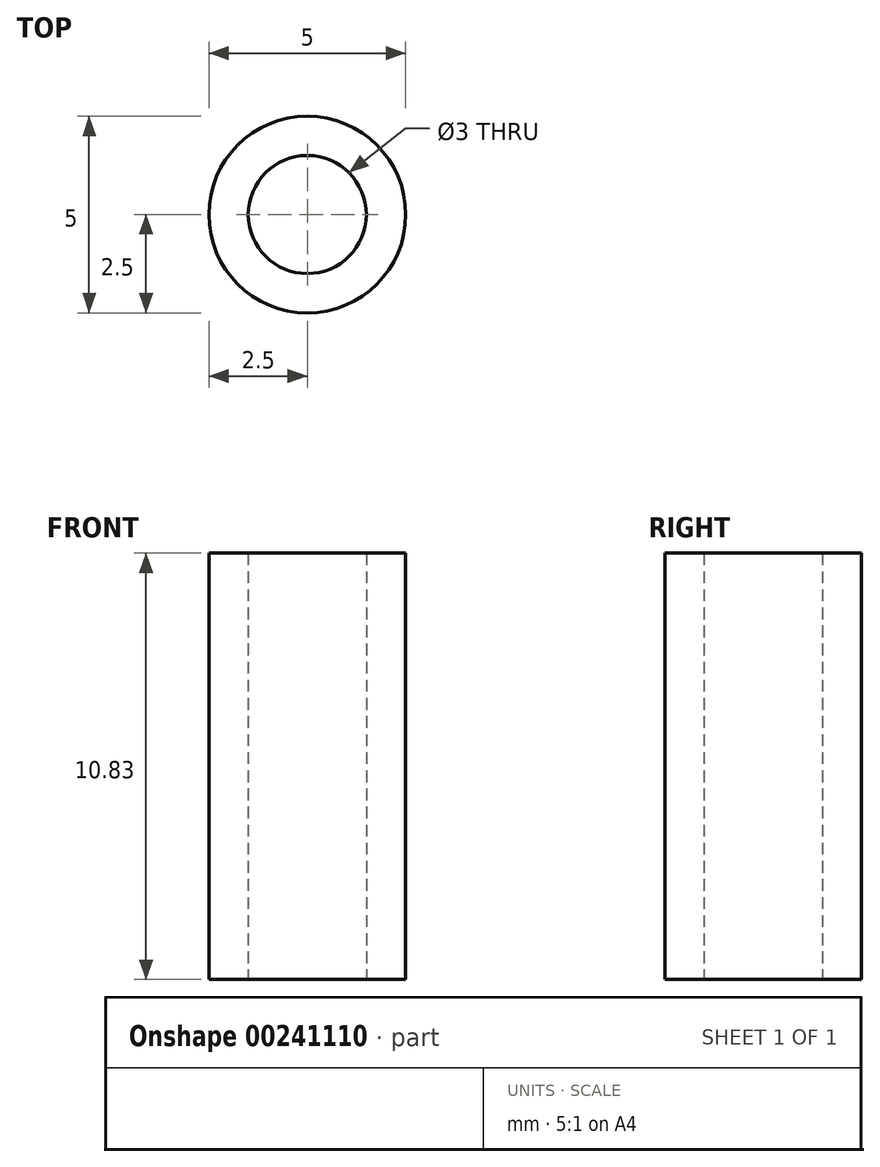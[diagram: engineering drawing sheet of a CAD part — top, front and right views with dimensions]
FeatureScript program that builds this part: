
annotation { "Feature Type Name" : "Feature", "Feature Type Description" : "" }
export const myFeature = defineFeature(function(context is Context, id is Id, definition is map)
    precondition{}
    {
        {
            var Q0;
            Q0=qCreatedBy(makeId("Top.planeOp"),FACE);
            var sketch = newSketch(context, id + "F0", { "sketchPlane" : qUnion([Q0])});
            skCircle(sketch, "E0", {"center": v(0, 0) * mm, "radius": 1.5 * mm});
            skCircle(sketch, "E1", {"center": v(0, 0) * mm, "radius": 2.5 * mm});
            skSolve(sketch);
        }
        {
            var Q0;
            Q0=qSketchRegion(id+"F0",true);
            extrude(context, id + "F1", {"entities" : qUnion([Q0]), "depth" : 10.83 * mm});
        }
    });
